# Revit family: UM304N Banco Neobarcino
name_source: partatom
category: Mobiliario
units: mm (PartAtom-declared; Revit-internal decimal feet)

## family parameters
Compartido = No
Corte con vacíos al cargar = No
Número OmniClass = 23.40.20.00
Punto de cálculo de habitación = No
Se basa en plano de trabajo = No
Siempre vertical = Sí
Título OmniClass = General Furniture and Specialties

## types (1)
- UM304N Banco Neobarcino
    Acabado Listones = Lignus, protector fungicida, insecticida e hidrófugo.
    Acabado bancada = Ferrus, proceso protector del hierro.Acabado imprimación epoxi y pintura poliéster en polvo color gris martelé.
    Accessibilidad = Sí
    Altura asiento = 460 mm  [stored 1.50919 ft]
    Altura total = 835 mm
    Ancho = 720 mm  [stored 2.3622 ft]
    Comentarios de tipo = Pies de fundición dúctil con tratamiento Ferrus, proceso protector del hierro, que garantiza una óptima resistencia a la corrosión. Acabado imprimación epoxi y pintura poliéster en polvo color gris martelé. Seis tablones de sección 110 x 35 mm de madera tropical tratada con Lignus, protector fungicida, insecticida e hidrófugo. Acabado color natural. Tornillos de acero inoxidable.Opcional: Se puede suministrar en madera con certificado FSC o en madera técnica.
    Fabricante = BENITO
    Ficha tecnica = http://www.benito.com
    Instalación = Anclaje recomendado: Tornillos M10 roscados a las bancadas y embebidos en hormigón.Tornillos no suministrados.
    Largo = 1800 mm  [stored 5.90551 ft]
    Material bancada = Fundición dúctil
    Material listones = Madera Tropical
    Modelo = Banco Neobarcino
    Referencia = UM304N
    URL = http://www.benito.com
    URL Producto = http://www.benito.com

note: [stored X ft] marks values corroborated as IEEE doubles in the binary element streams (Revit-internal decimal feet)

## geometry (parser evidence)
native form markers: Blend x4
no freeform markers — native parametric forms only
